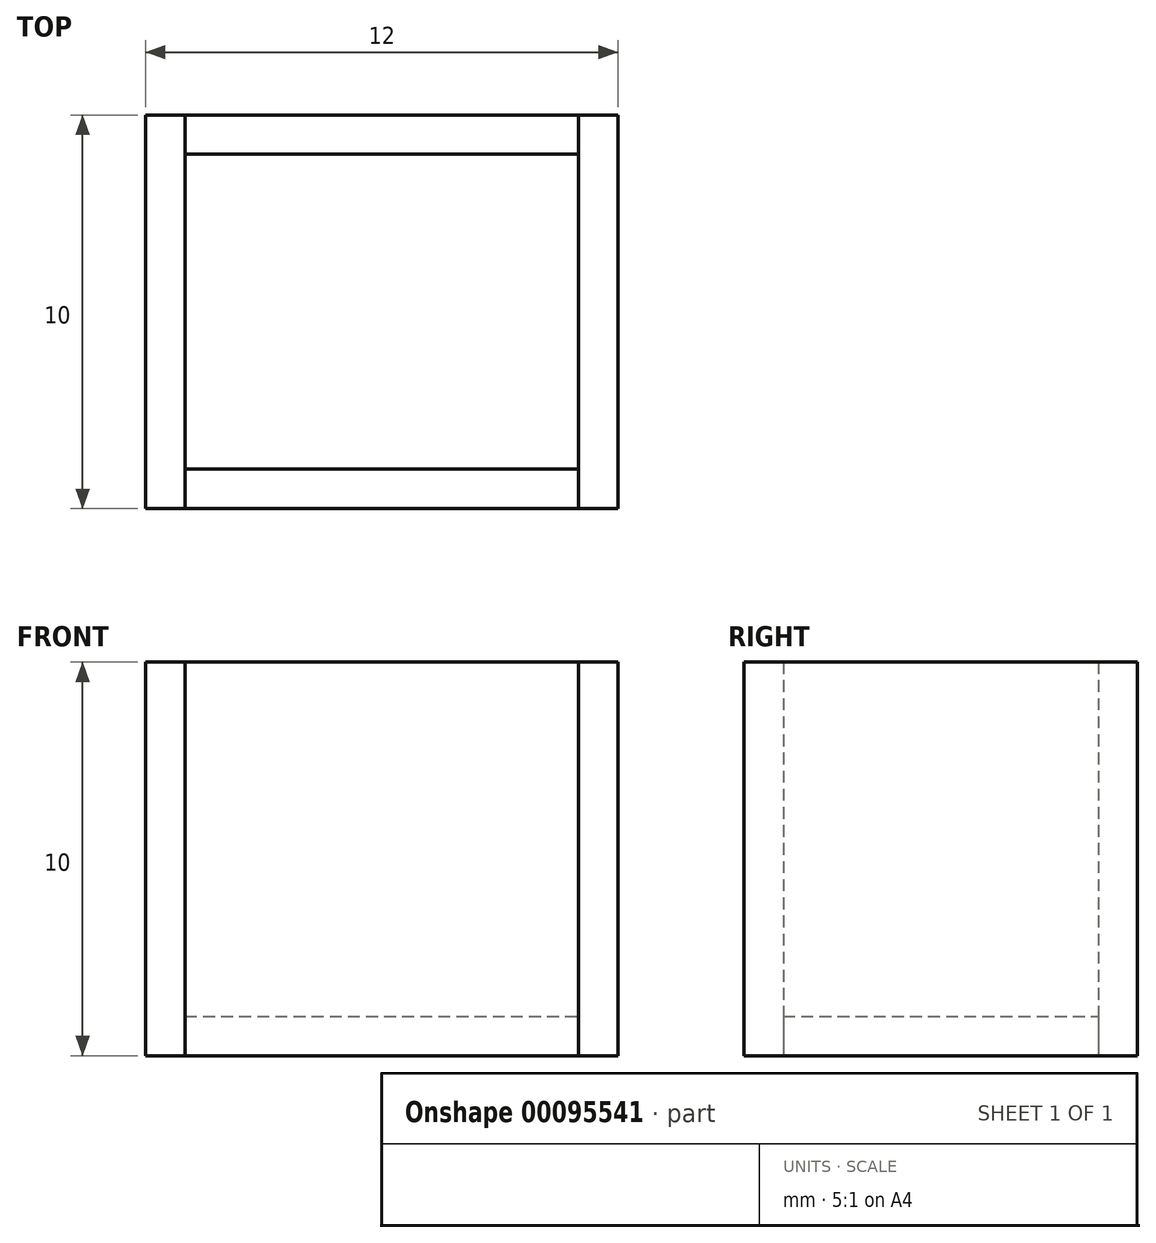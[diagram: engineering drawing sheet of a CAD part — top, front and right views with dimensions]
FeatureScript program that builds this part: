
annotation { "Feature Type Name" : "Feature", "Feature Type Description" : "" }
export const myFeature = defineFeature(function(context is Context, id is Id, definition is map)
    precondition{}
    {
        {
            var Q0;
            Q0=qCreatedBy(makeId("Top.planeOp"),FACE);
            var sketch = newSketch(context, id + "F0", { "sketchPlane" : qUnion([Q0])});
            skLineSegment(sketch, "E0.bottom", {"start": v(0, 0) * mm, "end": v(1, 0) * mm});
            skLineSegment(sketch, "E0.top", {"start": v(0, -10) * mm, "end": v(1, -10) * mm});
            skLineSegment(sketch, "E0.left", {"start": v(0, 0) * mm, "end": v(0, -10) * mm});
            skLineSegment(sketch, "E0.right", {"start": v(1, 0) * mm, "end": v(1, -10) * mm});
            skSolve(sketch);
        }
        {
            var Q0;
            Q0 = qSketchRegion(id + "F0", true);
            extrude(context, id + "F1", {"entities" : qUnion([Q0]), "depth" : 10 * mm});
        }
        {
            var Q0;
            Q0=qCreatedBy(makeId("Top.planeOp"),FACE);
            var sketch = newSketch(context, id + "F2", { "sketchPlane" : qUnion([Q0])});
            skLineSegment(sketch, "E1.bottom", {"start": v(1, -10) * mm, "end": v(11, -10) * mm});
            skLineSegment(sketch, "E1.top", {"start": v(1, -9) * mm, "end": v(11, -9) * mm});
            skLineSegment(sketch, "E1.left", {"start": v(1, -10) * mm, "end": v(1, -9) * mm});
            skLineSegment(sketch, "E1.right", {"start": v(11, -10) * mm, "end": v(11, -9) * mm});
            skSolve(sketch);
        }
        {
            var Q0;
            Q0 = qSketchRegion(id + "F2", true);
            extrude(context, id + "F3", {"entities" : qUnion([Q0]), "depth" : 10 * mm});
        }
        {
            var Q0;
            Q0=qCreatedBy(makeId("Top.planeOp"),FACE);
            var sketch = newSketch(context, id + "F4", { "sketchPlane" : qUnion([Q0])});
            skLineSegment(sketch, "E2.bottom", {"start": v(1, 0) * mm, "end": v(11, 0) * mm});
            skLineSegment(sketch, "E2.top", {"start": v(1, -1) * mm, "end": v(11, -1) * mm});
            skLineSegment(sketch, "E2.left", {"start": v(1, 0) * mm, "end": v(1, -1) * mm});
            skLineSegment(sketch, "E2.right", {"start": v(11, 0) * mm, "end": v(11, -1) * mm});
            skSolve(sketch);
        }
        {
            var Q0;
            Q0 = qSketchRegion(id + "F4", true);
            extrude(context, id + "F5", {"entities" : qUnion([Q0]), "depth" : 10 * mm});
        }
        {
            var Q0;
            Q0=qCreatedBy(makeId("Top.planeOp"),FACE);
            var sketch = newSketch(context, id + "F6", { "sketchPlane" : qUnion([Q0])});
            skLineSegment(sketch, "E3.bottom", {"start": v(11, 0) * mm, "end": v(12, 0) * mm});
            skLineSegment(sketch, "E3.top", {"start": v(11, -10) * mm, "end": v(12, -10) * mm});
            skLineSegment(sketch, "E3.left", {"start": v(11, 0) * mm, "end": v(11, -10) * mm});
            skLineSegment(sketch, "E3.right", {"start": v(12, 0) * mm, "end": v(12, -10) * mm});
            skSolve(sketch);
        }
        {
            var Q0;
            Q0 = qSketchRegion(id + "F6", true);
            extrude(context, id + "F7", {"entities" : qUnion([Q0]), "depth" : 10 * mm});
        }
        {
            var Q0;
            Q0=qCreatedBy(makeId("Top.planeOp"),FACE);
            var sketch = newSketch(context, id + "F8", { "sketchPlane" : qUnion([Q0])});
            skLineSegment(sketch, "E4.bottom", {"start": v(1, -9) * mm, "end": v(11, -9) * mm});
            skLineSegment(sketch, "E4.top", {"start": v(1, -1) * mm, "end": v(11, -1) * mm});
            skLineSegment(sketch, "E4.left", {"start": v(1, -9) * mm, "end": v(1, -1) * mm});
            skLineSegment(sketch, "E4.right", {"start": v(11, -9) * mm, "end": v(11, -1) * mm});
            skSolve(sketch);
        }
        {
            var Q0;
            Q0 = qSketchRegion(id + "F8", true);
            extrude(context, id + "F9", {"entities" : qUnion([Q0]), "depth" : 1 * mm});
        }
    });
